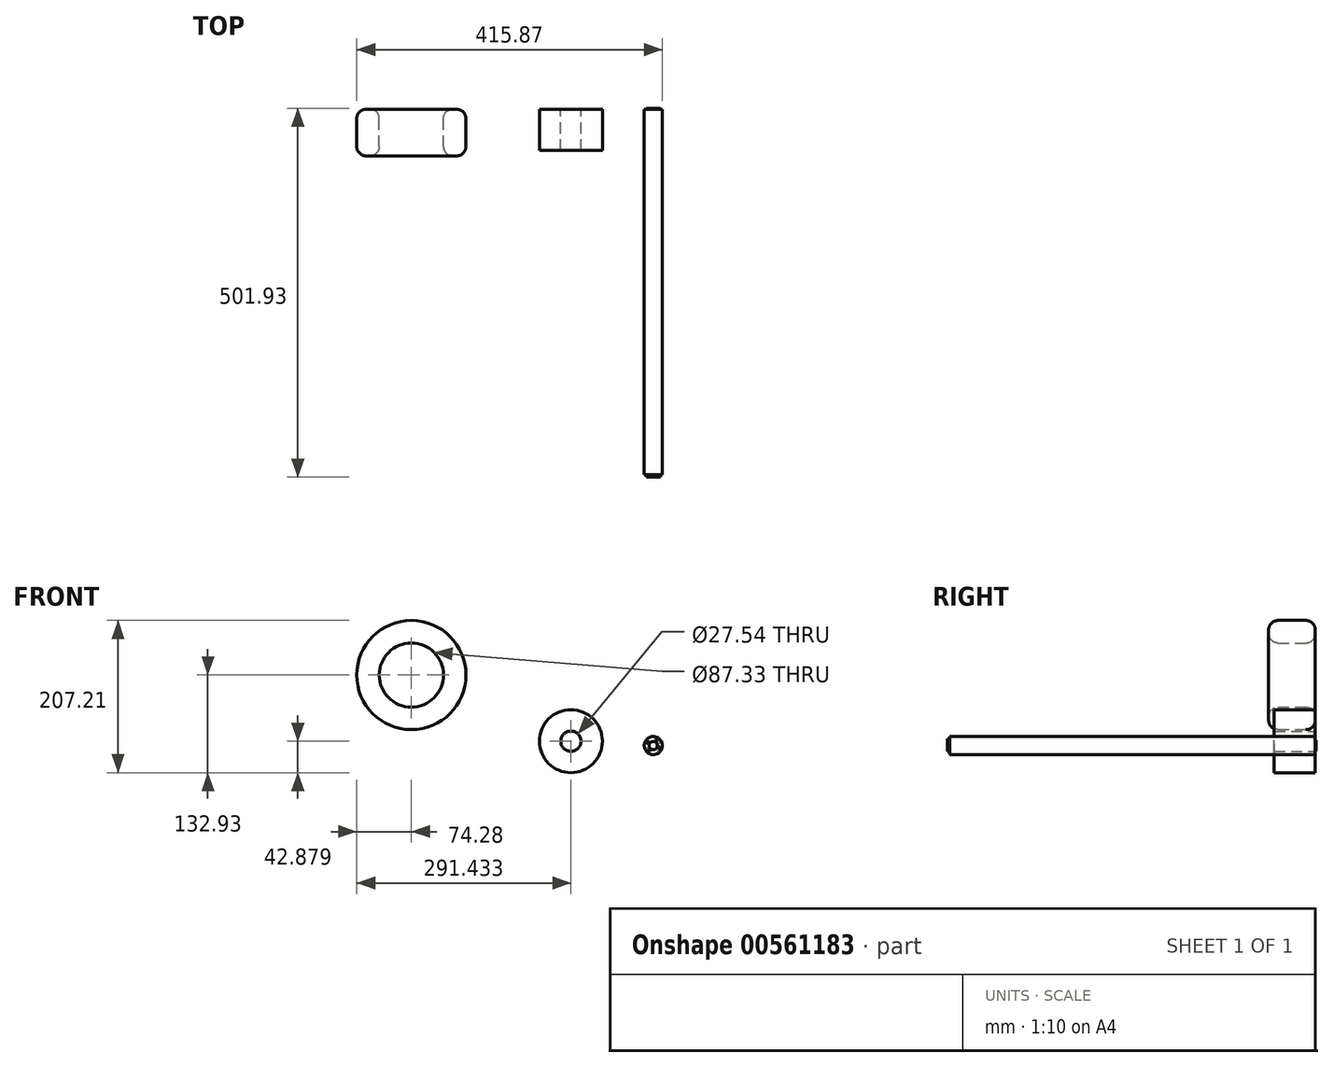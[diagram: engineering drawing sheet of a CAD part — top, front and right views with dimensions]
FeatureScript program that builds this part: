
annotation { "Feature Type Name" : "Feature", "Feature Type Description" : "" }
export const myFeature = defineFeature(function(context is Context, id is Id, definition is map)
    precondition{}
    {
        {
            var Q0;
            Q0=qCreatedBy(makeId("Front.planeOp"),FACE);
            var sketch = newSketch(context, id + "F0", { "sketchPlane" : qUnion([Q0])});
            skCircle(sketch, "E0", {"center": v(0, 0) * mm, "radius": 74.28 * mm});
            skSolve(sketch);
        }
        {
            var Q0;
            Q0=makeQuery(id+"F0.imprint","IMPRINT",FACE,{"disambiguationData":[TD([[makeQuery(id+"F0.imprint","IMPRINT",EDGE,{"derivedFrom":sQuery(id+"F0.wireOp",EDGE,"E0")}),1.0]])]});
            var sketch = newSketch(context, id + "F1", { "sketchPlane" : qUnion([Q0])});
            skCircle(sketch, "E1", {"center": v(0, 0) * mm, "radius": 43.67 * mm});
            skSolve(sketch);
        }
        {
            var Q0;
            Q0=makeQuery(id+"F1.imprint","IMPRINT",FACE,{"disambiguationData":[TD([[makeQuery(id+"F1.imprint","IMPRINT",EDGE,{"derivedFrom":sQuery(id+"F1.wireOp",EDGE,"E1")}),-1.0]])]});
            extrude(context, id + "F2", {"entities" : qUnion([Q0]), "depth" : 63.5 * mm, "offsetDistance" : 25.4 * mm});
        }
        {
            var Q0;
            Q0=makeQuery(id+"F2.opExtrude","CAP_EDGE",EDGE,{"disambiguationData":[OSD([sQuery(id+"F0.wireOp",EDGE,"E0")])],"isStart":false});
            var Q1;
            Q1=makeQuery(id+"F2.opExtrude","CAP_EDGE",EDGE,{"disambiguationData":[OSD([sQuery(id+"F0.wireOp",EDGE,"E0")])],"isStart":true});
            var Q2;
            Q2=makeQuery(id+"F2.opExtrude","CAP_EDGE",EDGE,{"disambiguationData":[OSD([sQuery(id+"F1.wireOp",EDGE,"E1")])],"isStart":false});
            var Q3;
            Q3=makeQuery(id+"F2.opExtrude","CAP_EDGE",EDGE,{"disambiguationData":[OSD([sQuery(id+"F1.wireOp",EDGE,"E1")])],"isStart":true});
            fillet(context, id + "F3", {"entities" : qUnion([Q0, Q1, Q2, Q3]), "radius" : 12.7 * mm, "tangentPropagation" : true, "allowEdgeOverflow" : false});
        }
        {
            var Q0;
            Q0=qCreatedBy(makeId("Front.planeOp"),FACE);
            var sketch = newSketch(context, id + "F4", { "sketchPlane" : qUnion([Q0])});
            skCircle(sketch, "E2", {"center": v(217.15, -90.05) * mm, "radius": 42.88 * mm});
            skCircle(sketch, "E3", {"center": v(217.15, -90.05) * mm, "radius": 13.77 * mm});
            skSolve(sketch);
        }
        {
            var Q0;
            Q0=makeQuery(id+"F4.imprint","IMPRINT",FACE,{"disambiguationData":[TD([[makeQuery(id+"F4.imprint","IMPRINT",EDGE,{"derivedFrom":sQuery(id+"F4.wireOp",EDGE,"E2")}),1.0]])]});
            extrude(context, id + "F5", {"entities" : qUnion([Q0]), "depth" : 55.88 * mm, "offsetDistance" : 25.4 * mm});
        }
        {
            var Q0;
            Q0=makeQuery(id+"F5.opExtrude","CAP_FACE",FACE,{"disambiguationData":[OSD([sQuery(id+"F4.wireOp",EDGE,"E2"),sQuery(id+"F4.wireOp",EDGE,"E3")])],"isStart":false});
            var sketch = newSketch(context, id + "F6", { "sketchPlane" : qUnion([Q0])});
            skSolve(sketch);
        }
        {
            var Q0;
            Q0=makeQuery(id+"F6.imprint","IMPRINT",FACE,{"disambiguationData":[TD([[makeQuery(id+"F6.imprint","IMPRINT",EDGE,{"derivedFrom":makeQuery(id+"F5.opExtrude","CAP_EDGE",EDGE,{"disambiguationData":[OSD([sQuery(id+"F4.wireOp",EDGE,"E2")])],"isStart":false})}),1.0]])]});
            var sketch = newSketch(context, id + "F7", { "sketchPlane" : qUnion([Q0])});
            skLineSegment(sketch, "E4", {"start": v(219.37, -47.74) * mm, "end": v(219.37, -75.41) * mm});
            skLineSegment(sketch, "E5", {"start": v(219.37, -75.41) * mm, "end": v(236.25, -52.58) * mm});
            skLineSegment(sketch, "E6", {"start": v(236.25, -52.58) * mm, "end": v(219.37, -47.74) * mm});
            skLineSegment(sketch, "E7", {"start": v(197.4, -127.9) * mm, "end": v(213.67, -103.69) * mm});
            skLineSegment(sketch, "E8", {"start": v(213.67, -103.69) * mm, "end": v(212.24, -132.37) * mm});
            skLineSegment(sketch, "E9", {"start": v(212.24, -132.37) * mm, "end": v(197.4, -127.9) * mm});
            skLineSegment(sketch, "E10", {"start": v(259.65, -91.08) * mm, "end": v(231.17, -91.08) * mm});
            skLineSegment(sketch, "E11", {"start": v(231.17, -91.08) * mm, "end": v(256.1, -106.54) * mm});
            skLineSegment(sketch, "E12", {"start": v(256.1, -106.54) * mm, "end": v(259.65, -91.08) * mm});
            skLineSegment(sketch, "E13", {"start": v(174.61, -86.8) * mm, "end": v(202.9, -86.8) * mm});
            skLineSegment(sketch, "E14", {"start": v(202.9, -86.8) * mm, "end": v(177.62, -71.95) * mm});
            skLineSegment(sketch, "E15", {"start": v(177.62, -71.95) * mm, "end": v(174.61, -86.8) * mm});
            skSolve(sketch);
        }
        {
            var Q0;
            Q0=sQuery(id+"F7.wireOp",EDGE,"E11");
            var Q1;
            Q1=sQuery(id+"F7.wireOp",EDGE,"E10");
            var Q2;
            Q2=sQuery(id+"F7.wireOp",EDGE,"E12");
            var Q3;
            Q3=sQuery(id+"F7.wireOp",EDGE,"E5");
            var Q4;
            Q4=sQuery(id+"F7.wireOp",EDGE,"E6");
            var Q5;
            Q5=sQuery(id+"F7.wireOp",EDGE,"E4");
            var Q6;
            Q6=sQuery(id+"F7.wireOp",EDGE,"E14");
            var Q7;
            Q7=sQuery(id+"F7.wireOp",EDGE,"E13");
            var Q8;
            Q8=sQuery(id+"F7.wireOp",EDGE,"E15");
            var Q9;
            Q9=sQuery(id+"F7.wireOp",EDGE,"E8");
            var Q10;
            Q10=sQuery(id+"F7.wireOp",EDGE,"E7");
            var Q11;
            Q11=sQuery(id+"F7.wireOp",EDGE,"E9");
            extrude(context, id + "F8", {"bodyType" : ToolBodyType.SURFACE, "surfaceEntities" : qUnion([Q0, Q1, Q2, Q3, Q4, Q5, Q6, Q7, Q8, Q9, Q10, Q11]), "depth" : 5.08 * mm, "offsetDistance" : 25.4 * mm});
        }
        {
            var Q0;
            Q0=qCreatedBy(makeId("Front.planeOp"),FACE);
            var sketch = newSketch(context, id + "F9", { "sketchPlane" : qUnion([Q0])});
            skCircle(sketch, "E16", {"center": v(329.23, -95.98) * mm, "radius": 12.36 * mm});
            skSolve(sketch);
        }
        {
            var Q0;
            Q0 = qSketchRegion(id + "F9", true);
            extrude(context, id + "F10", {"entities" : qUnion([Q0]), "depth" : 497.6 * mm, "offsetDistance" : 25.4 * mm});
        }
        {
            var Q0;
            Q0=makeQuery(id+"F10.opExtrude","CAP_FACE",FACE,{"disambiguationData":[OSD([sQuery(id+"F9.wireOp",EDGE,"E16")])],"isStart":false});
            var sketch = newSketch(context, id + "F11", { "sketchPlane" : qUnion([Q0])});
            skCircle(sketch, "E17", {"center": v(329.23, -95.98) * mm, "radius": 5.6 * mm});
            skCircle(sketch, "E18.cCircle", {"center": v(321.47, -91.23) * mm, "radius": 1.7 * mm, "construction": true});
            skLineSegment(sketch, "E18.0", {"start": v(322.99, -91.98) * mm, "end": v(321.57, -92.91) * mm});
            skLineSegment(sketch, "E18.1", {"start": v(321.57, -92.91) * mm, "end": v(320.06, -92.16) * mm});
            skLineSegment(sketch, "E18.2", {"start": v(320.06, -92.16) * mm, "end": v(319.96, -90.47) * mm});
            skLineSegment(sketch, "E18.3", {"start": v(319.96, -90.47) * mm, "end": v(321.37, -89.54) * mm});
            skLineSegment(sketch, "E18.4", {"start": v(321.37, -89.54) * mm, "end": v(322.88, -90.3) * mm});
            skLineSegment(sketch, "E18.5", {"start": v(322.88, -90.3) * mm, "end": v(322.99, -91.98) * mm});
            skCircle(sketch, "E19.cCircle", {"center": v(323.24, -102.47) * mm, "radius": 1.61 * mm, "construction": true});
            skLineSegment(sketch, "E19.0", {"start": v(324.85, -102.42) * mm, "end": v(324.09, -103.84) * mm});
            skLineSegment(sketch, "E19.1", {"start": v(324.09, -103.84) * mm, "end": v(322.47, -103.9) * mm});
            skLineSegment(sketch, "E19.2", {"start": v(322.47, -103.9) * mm, "end": v(321.62, -102.52) * mm});
            skLineSegment(sketch, "E19.3", {"start": v(321.62, -102.52) * mm, "end": v(322.39, -101.1) * mm});
            skLineSegment(sketch, "E19.4", {"start": v(322.39, -101.1) * mm, "end": v(324, -101.05) * mm});
            skLineSegment(sketch, "E19.5", {"start": v(324, -101.05) * mm, "end": v(324.85, -102.42) * mm});
            skCircle(sketch, "E20.cCircle", {"center": v(337.46, -98.79) * mm, "radius": 1.66 * mm, "construction": true});
            skLineSegment(sketch, "E20.0", {"start": v(339.12, -98.84) * mm, "end": v(338.25, -100.26) * mm});
            skLineSegment(sketch, "E20.1", {"start": v(338.25, -100.26) * mm, "end": v(336.58, -100.2) * mm});
            skLineSegment(sketch, "E20.2", {"start": v(336.58, -100.2) * mm, "end": v(335.8, -98.74) * mm});
            skLineSegment(sketch, "E20.3", {"start": v(335.8, -98.74) * mm, "end": v(336.67, -97.32) * mm});
            skLineSegment(sketch, "E20.4", {"start": v(336.67, -97.32) * mm, "end": v(338.33, -97.37) * mm});
            skLineSegment(sketch, "E20.5", {"start": v(338.33, -97.37) * mm, "end": v(339.12, -98.84) * mm});
            skCircle(sketch, "E21.cCircle", {"center": v(333.68, -88.55) * mm, "radius": 1.6 * mm, "construction": true});
            skLineSegment(sketch, "E21.0", {"start": v(334.73, -87.34) * mm, "end": v(335.25, -88.87) * mm});
            skLineSegment(sketch, "E21.1", {"start": v(335.25, -88.87) * mm, "end": v(334.2, -90.08) * mm});
            skLineSegment(sketch, "E21.2", {"start": v(334.2, -90.08) * mm, "end": v(332.62, -89.76) * mm});
            skLineSegment(sketch, "E21.3", {"start": v(332.62, -89.76) * mm, "end": v(332.1, -88.24) * mm});
            skLineSegment(sketch, "E21.4", {"start": v(332.1, -88.24) * mm, "end": v(333.16, -87.03) * mm});
            skLineSegment(sketch, "E21.5", {"start": v(333.16, -87.03) * mm, "end": v(334.73, -87.34) * mm});
            skSolve(sketch);
        }
        {
            var Q0;
            Q0=makeQuery(id+"F11.imprint","IMPRINT",FACE,{"disambiguationData":[TD([[makeQuery(id+"F11.imprint","IMPRINT",EDGE,{"derivedFrom":sQuery(id+"F11.wireOp",EDGE,"E21.0")}),-1.0]])]});
            var Q1;
            Q1=makeQuery(id+"F11.imprint","IMPRINT",FACE,{"disambiguationData":[TD([[makeQuery(id+"F11.imprint","IMPRINT",EDGE,{"derivedFrom":sQuery(id+"F11.wireOp",EDGE,"E20.0")}),-1.0]])]});
            var Q2;
            Q2=makeQuery(id+"F11.imprint","IMPRINT",FACE,{"disambiguationData":[TD([[makeQuery(id+"F11.imprint","IMPRINT",EDGE,{"derivedFrom":sQuery(id+"F11.wireOp",EDGE,"E19.0")}),-1.0]])]});
            var Q3;
            Q3=makeQuery(id+"F11.imprint","IMPRINT",FACE,{"disambiguationData":[TD([[makeQuery(id+"F11.imprint","IMPRINT",EDGE,{"derivedFrom":sQuery(id+"F11.wireOp",EDGE,"E18.0")}),-1.0]])]});
            var Q4;
            Q4=makeQuery(id+"F11.imprint","IMPRINT",FACE,{"disambiguationData":[TD([[makeQuery(id+"F11.imprint","IMPRINT",EDGE,{"derivedFrom":sQuery(id+"F11.wireOp",EDGE,"E17")}),1.0]])]});
            extrude(context, id + "F12", {"entities" : qUnion([Q0, Q1, Q2, Q3, Q4]), "operationType" : NewBodyOperationType.ADD, "depth" : 3.1 * mm, "offsetDistance" : 25.4 * mm});
        }
        {
            var Q0;
            Q0=makeQuery(id+"F10.opExtrude","CAP_FACE",FACE,{"disambiguationData":[OSD([sQuery(id+"F9.wireOp",EDGE,"E16")])],"isStart":true});
            var sketch = newSketch(context, id + "F13", { "sketchPlane" : qUnion([Q0])});
            skCircle(sketch, "E22", {"center": v(-329.23, -95.98) * mm, "radius": 6.17 * mm});
            skCircle(sketch, "E23.cCircle", {"center": v(-321.58, -90.25) * mm, "radius": 1.46 * mm, "construction": true});
            skLineSegment(sketch, "E23.0", {"start": v(-320.55, -91.28) * mm, "end": v(-321.95, -91.65) * mm});
            skLineSegment(sketch, "E23.1", {"start": v(-321.95, -91.65) * mm, "end": v(-322.99, -90.62) * mm});
            skLineSegment(sketch, "E23.2", {"start": v(-322.99, -90.62) * mm, "end": v(-322.6, -89.22) * mm});
            skLineSegment(sketch, "E23.3", {"start": v(-322.6, -89.22) * mm, "end": v(-321.2, -88.84) * mm});
            skLineSegment(sketch, "E23.4", {"start": v(-321.2, -88.84) * mm, "end": v(-320.17, -89.87) * mm});
            skLineSegment(sketch, "E23.5", {"start": v(-320.17, -89.87) * mm, "end": v(-320.55, -91.28) * mm});
            skCircle(sketch, "E24.cCircle", {"center": v(-337.26, -91.14) * mm, "radius": 1.46 * mm, "construction": true});
            skLineSegment(sketch, "E24.0", {"start": v(-336.6, -92.44) * mm, "end": v(-338.05, -92.37) * mm});
            skLineSegment(sketch, "E24.1", {"start": v(-338.05, -92.37) * mm, "end": v(-338.73, -91.08) * mm});
            skLineSegment(sketch, "E24.2", {"start": v(-338.73, -91.08) * mm, "end": v(-337.94, -89.84) * mm});
            skLineSegment(sketch, "E24.3", {"start": v(-337.94, -89.84) * mm, "end": v(-336.47, -89.91) * mm});
            skLineSegment(sketch, "E24.4", {"start": v(-336.47, -89.91) * mm, "end": v(-335.8, -91.21) * mm});
            skLineSegment(sketch, "E24.5", {"start": v(-335.8, -91.21) * mm, "end": v(-336.6, -92.44) * mm});
            skCircle(sketch, "E25.cCircle", {"center": v(-335.82, -102.17) * mm, "radius": 1.52 * mm, "construction": true});
            skLineSegment(sketch, "E25.0", {"start": v(-334.3, -102.26) * mm, "end": v(-335.14, -103.53) * mm});
            skLineSegment(sketch, "E25.1", {"start": v(-335.14, -103.53) * mm, "end": v(-336.66, -103.44) * mm});
            skLineSegment(sketch, "E25.2", {"start": v(-336.66, -103.44) * mm, "end": v(-337.34, -102.08) * mm});
            skLineSegment(sketch, "E25.3", {"start": v(-337.34, -102.08) * mm, "end": v(-336.5, -100.81) * mm});
            skLineSegment(sketch, "E25.4", {"start": v(-336.5, -100.81) * mm, "end": v(-334.99, -100.9) * mm});
            skLineSegment(sketch, "E25.5", {"start": v(-334.99, -100.9) * mm, "end": v(-334.3, -102.26) * mm});
            skCircle(sketch, "E26.cCircle", {"center": v(-321.49, -100.6) * mm, "radius": 1.5 * mm, "construction": true});
            skLineSegment(sketch, "E26.0", {"start": v(-320.73, -101.9) * mm, "end": v(-322.23, -101.9) * mm});
            skLineSegment(sketch, "E26.1", {"start": v(-322.23, -101.9) * mm, "end": v(-323, -100.6) * mm});
            skLineSegment(sketch, "E26.2", {"start": v(-323, -100.6) * mm, "end": v(-322.25, -99.3) * mm});
            skLineSegment(sketch, "E26.3", {"start": v(-322.25, -99.3) * mm, "end": v(-320.74, -99.3) * mm});
            skLineSegment(sketch, "E26.4", {"start": v(-320.74, -99.3) * mm, "end": v(-319.98, -100.59) * mm});
            skLineSegment(sketch, "E26.5", {"start": v(-319.98, -100.59) * mm, "end": v(-320.73, -101.9) * mm});
            skSolve(sketch);
        }
        {
            var Q0;
            Q0 = qSketchRegion(id + "F13", true);
            extrude(context, id + "F14", {"entities" : qUnion([Q0]), "operationType" : NewBodyOperationType.ADD, "depth" : 1.22 * mm, "offsetDistance" : 25.4 * mm});
        }
    });
